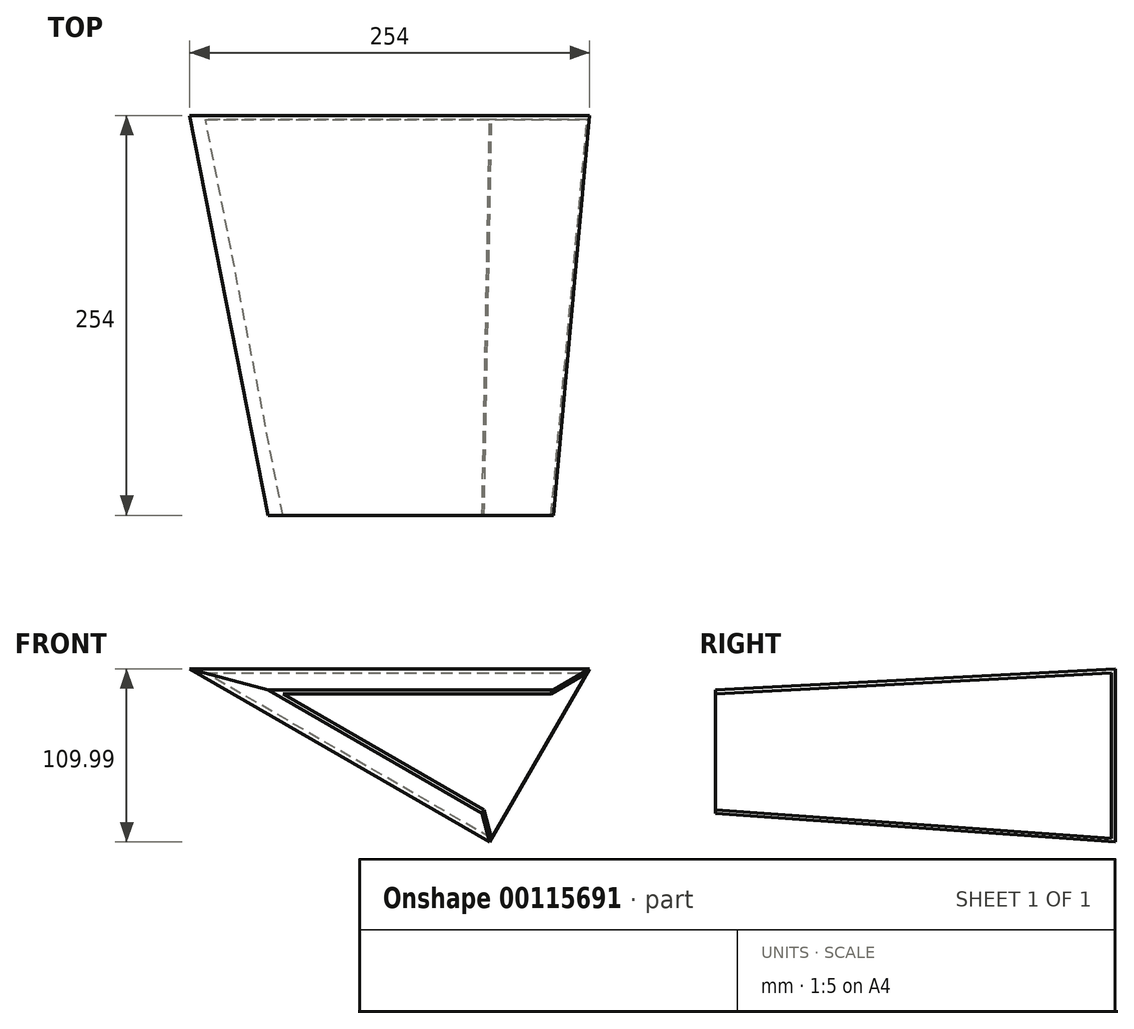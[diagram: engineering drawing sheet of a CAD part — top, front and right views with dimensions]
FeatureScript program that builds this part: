
annotation { "Feature Type Name" : "Feature", "Feature Type Description" : "" }
export const myFeature = defineFeature(function(context is Context, id is Id, definition is map)
    precondition{}
    {
        {
            var Q0;
            Q0=qCreatedBy(makeId("Front.planeOp"),FACE);
            var sketch = newSketch(context, id + "F0", { "sketchPlane" : qUnion([Q0])});
            skLineSegment(sketch, "E0", {"start": v(0, 0) * mm, "end": v(254, 0) * mm});
            skLineSegment(sketch, "E1", {"start": v(254, 0) * mm, "end": v(190.5, -109.99) * mm});
            skLineSegment(sketch, "E2", {"start": v(190.5, -109.99) * mm, "end": v(0, 0) * mm});
            skSolve(sketch);
        }
        {
            var Q0;
            Q0=makeQuery(id+"F0.imprint","IMPRINT",FACE,{"disambiguationData":[TD([[makeQuery(id+"F0.imprint","IMPRINT",EDGE,{"derivedFrom":sQuery(id+"F0.wireOp",EDGE,"E0")}),-1.0]])]});
            extrude(context, id + "F1", {"entities" : qUnion([Q0]), "depth" : 254 * mm, "hasDraft" : true, "draftAngle" : 3 * degree, "draftPullDirection" : true});
        }
        {
            var Q0;
            Q0=makeQuery(id+"F1.opExtrude","CAP_FACE",FACE,{"disambiguationData":[OSD([sQuery(id+"F0.wireOp",EDGE,"E0"),sQuery(id+"F0.wireOp",EDGE,"E1"),sQuery(id+"F0.wireOp",EDGE,"E2")])],"isStart":false});
            var Q1;
            Q1=makeQuery(id+"F1.opExtrude","SWEPT_FACE",FACE,{"disambiguationData":[OSD([sQuery(id+"F0.wireOp",EDGE,"E1")])]});
            shell(context, id + "F2", {"entities" : qUnion([Q0, Q1]), "thickness" : 2.54 * mm});
        }
    });
